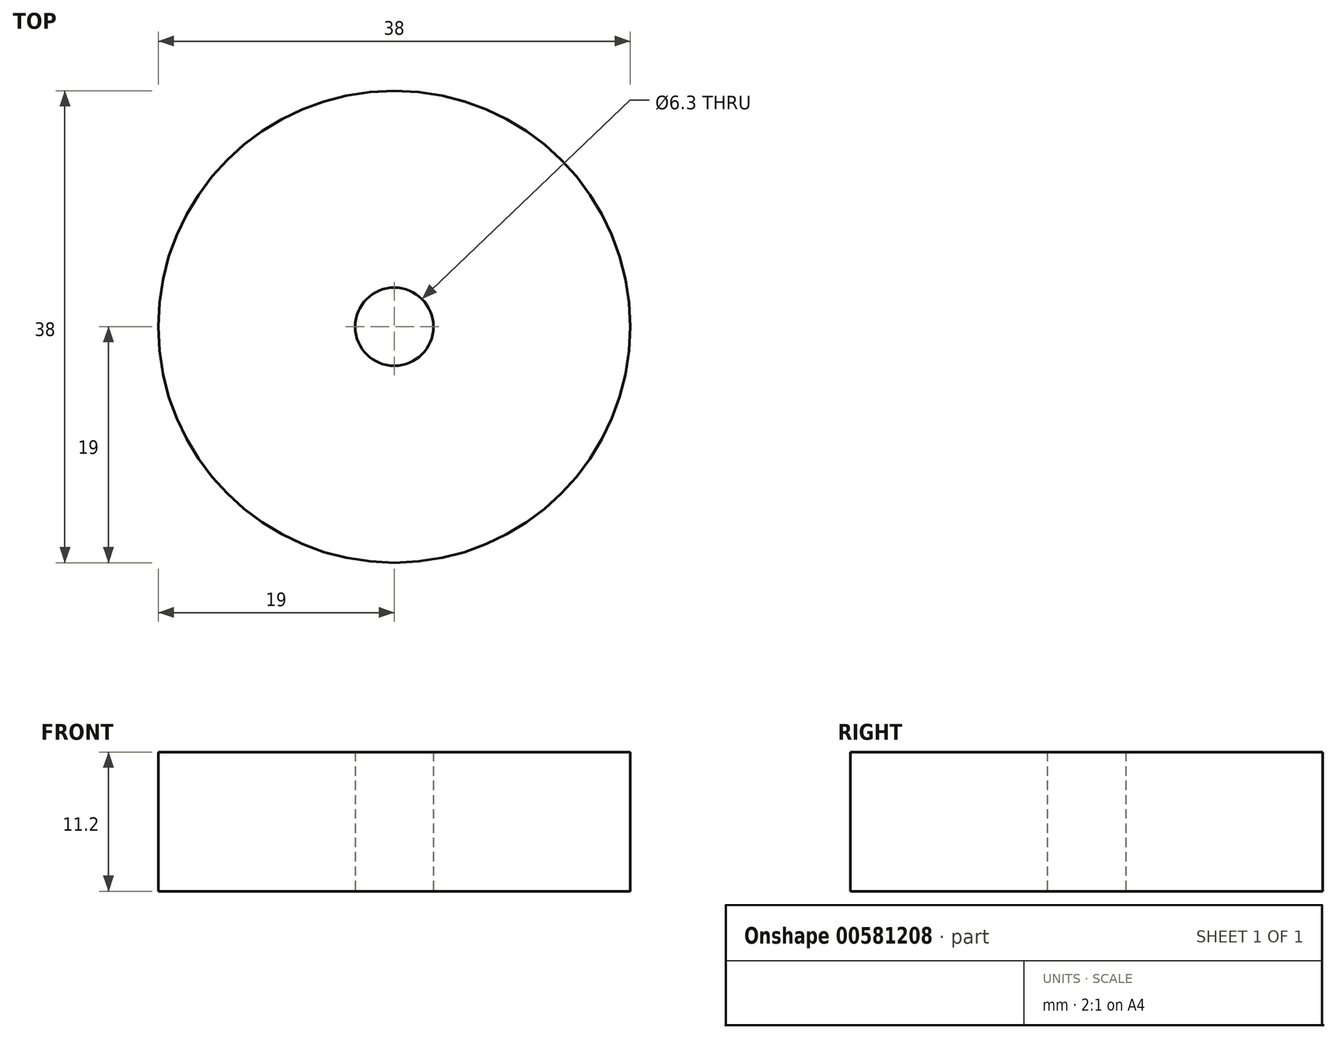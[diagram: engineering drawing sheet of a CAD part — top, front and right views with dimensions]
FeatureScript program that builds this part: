
annotation { "Feature Type Name" : "Feature", "Feature Type Description" : "" }
export const myFeature = defineFeature(function(context is Context, id is Id, definition is map)
    precondition{}
    {
        {
            var Q0;
            Q0=qCreatedBy(makeId("Top.planeOp"),FACE);
            var sketch = newSketch(context, id + "F0", { "sketchPlane" : qUnion([Q0])});
            skCircle(sketch, "E0", {"center": v(0, 0) * mm, "radius": 19 * mm});
            skCircle(sketch, "E1", {"center": v(0, 0) * mm, "radius": 3.15 * mm});
            skSolve(sketch);
        }
        {
            var Q0;
            Q0 = qSketchRegion(id + "F0", true);
            extrude(context, id + "F1", {"entities" : qUnion([Q0]), "depth" : 11.2 * mm, "offsetDistance" : 25 * mm});
        }
    });
